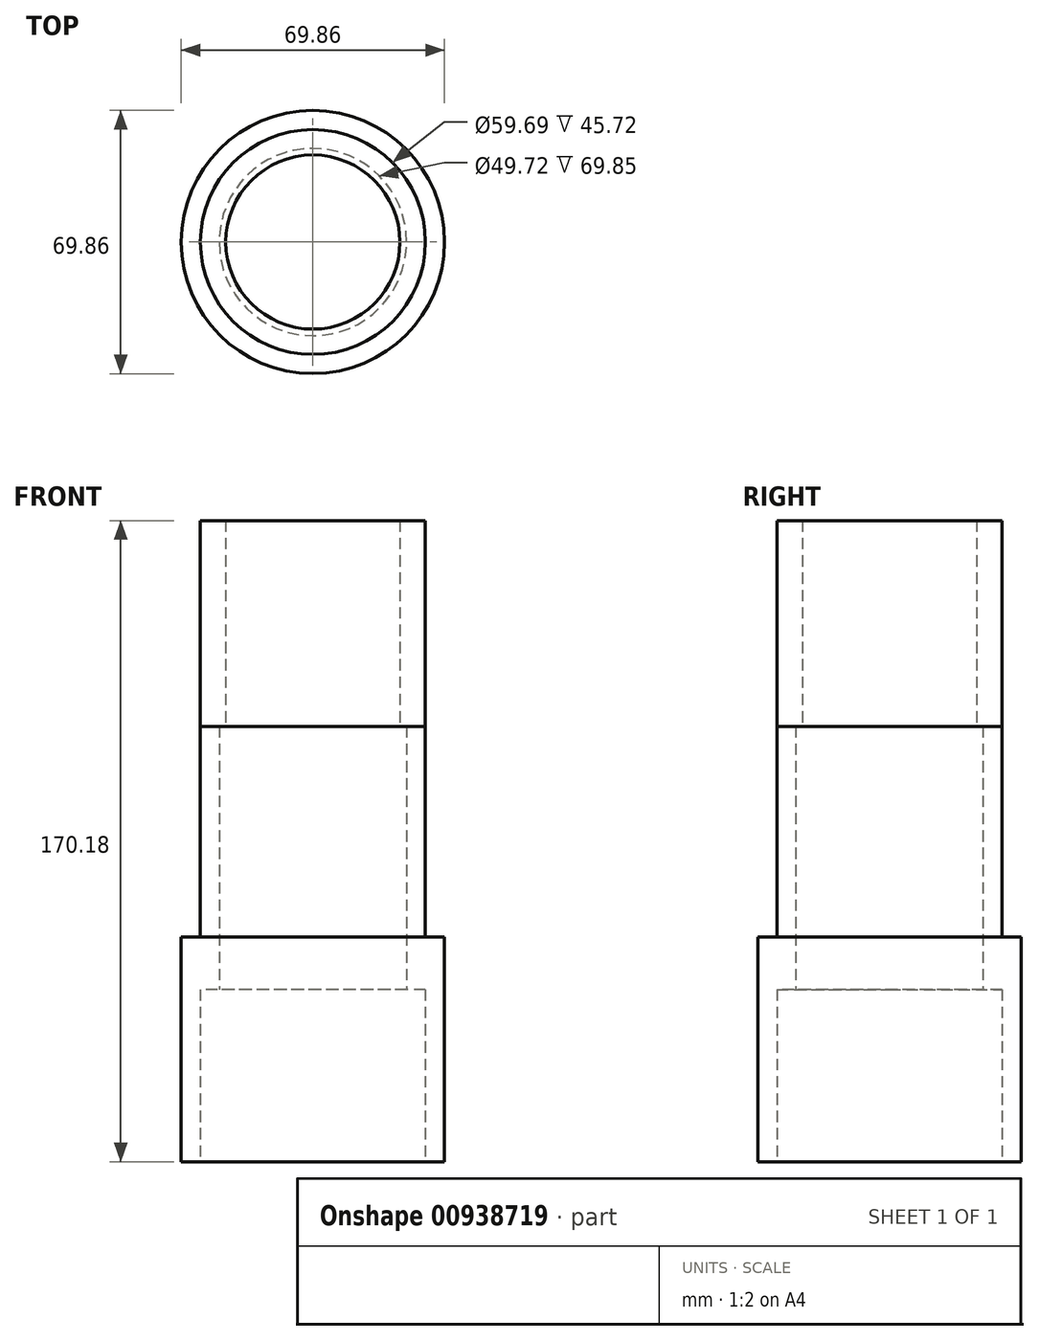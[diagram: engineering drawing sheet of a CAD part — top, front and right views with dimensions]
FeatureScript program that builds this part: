
annotation { "Feature Type Name" : "Feature", "Feature Type Description" : "" }
export const myFeature = defineFeature(function(context is Context, id is Id, definition is map)
    precondition{}
    {
        {
            var Q0;
            Q0=qCreatedBy(makeId("Top.planeOp"),FACE);
            var sketch = newSketch(context, id + "F0", { "sketchPlane" : qUnion([Q0])});
            skCircle(sketch, "E0", {"center": v(0, 0) * mm, "radius": 34.93 * mm});
            skCircle(sketch, "E1", {"center": v(0, 0) * mm, "radius": 29.85 * mm});
            skSolve(sketch);
        }
        {
            var Q0;
            Q0 = qSketchRegion(id + "F0", true);
            extrude(context, id + "F1", {"entities" : qUnion([Q0]), "depth" : 59.69 * mm, "offsetDistance" : 25.4 * mm});
        }
        {
            var Q0;
            Q0=qCreatedBy(makeId("Top.planeOp"),FACE);
            cPlane(context, id + "F2", {"entities" : qUnion([Q0]), "cplaneType" : CPlaneType.OFFSET, "offset" : 38.1 * mm, "width" : 152.4 * mm, "height" : 152.4 * mm});
        }
        {
            var Q0;
            Q0=qCreatedBy(makeId("Top.planeOp"),FACE);
            cPlane(context, id + "F3", {"entities" : qUnion([Q0]), "cplaneType" : CPlaneType.OFFSET, "offset" : 45.72 * mm, "width" : 152.4 * mm, "height" : 152.4 * mm});
        }
        {
            var Q0;
            Q0=qCreatedBy(id+"F2.planeOp",FACE);
            var sketch = newSketch(context, id + "F4", { "sketchPlane" : qUnion([Q0])});
            skCircle(sketch, "E2", {"center": v(0, 0) * mm, "radius": 29.84 * mm});
            skSolve(sketch);
        }
        {
            var Q0;
            Q0=qCreatedBy(id+"F3.planeOp",FACE);
            var sketch = newSketch(context, id + "F5", { "sketchPlane" : qUnion([Q0])});
            skCircle(sketch, "E3", {"center": v(0, 0) * mm, "radius": 24.77 * mm});
            skSolve(sketch);
        }
        {
            var Q0;
            Q0=sQuery(id+"F4.wireOp",EDGE,"E2");
            var Q1;
            Q1=sQuery(id+"F5.wireOp",EDGE,"E3");
            loft(context, id + "F6", {"bodyType" : ToolBodyType.SURFACE, "wireProfilesArray" : [{ "wireProfileEntities" : qUnion([Q0]) }, { "wireProfileEntities" : qUnion([Q1]) }]});
        }
        {
            var Q0;
            Q0=qCreatedBy(id+"F3.planeOp",FACE);
            var sketch = newSketch(context, id + "F7", { "sketchPlane" : qUnion([Q0])});
            skCircle(sketch, "E4", {"center": v(0, 0) * mm, "radius": 29.85 * mm});
            skCircle(sketch, "E5", {"center": v(0, 0) * mm, "radius": 24.86 * mm});
            skSolve(sketch);
        }
        {
            var Q0;
            Q0 = qSketchRegion(id + "F7", true);
            extrude(context, id + "F8", {"entities" : qUnion([Q0]), "operationType" : NewBodyOperationType.ADD, "depth" : 69.85 * mm, "offsetDistance" : 25.4 * mm});
        }
        {
            var Q0;
            Q0=qCreatedBy(makeId("Top.planeOp"),FACE);
            cPlane(context, id + "F9", {"entities" : qUnion([Q0]), "cplaneType" : CPlaneType.OFFSET, "offset" : 170.18 * mm, "width" : 152.4 * mm, "height" : 152.4 * mm});
        }
        {
            var Q0;
            Q0=qCreatedBy(id+"F9.planeOp",FACE);
            cPlane(context, id + "F10", {"entities" : qUnion([Q0]), "cplaneType" : CPlaneType.OFFSET, "offset" : 54.6 * mm, "oppositeDirection" : true, "width" : 152.4 * mm, "height" : 152.4 * mm});
        }
        {
            var Q0;
            Q0=qCreatedBy(id+"F10.planeOp",FACE);
            cPlane(context, id + "F11", {"entities" : qUnion([Q0]), "cplaneType" : CPlaneType.OFFSET, "offset" : 7.62 * mm, "oppositeDirection" : true, "width" : 152.4 * mm, "height" : 152.4 * mm});
        }
        {
            var Q0;
            Q0=qCreatedBy(id+"F11.planeOp",FACE);
            var sketch = newSketch(context, id + "F12", { "sketchPlane" : qUnion([Q0])});
            skCircle(sketch, "E6", {"center": v(0, 0) * mm, "radius": 24.77 * mm});
            skSolve(sketch);
        }
        {
            var Q0;
            Q0=qCreatedBy(id+"F10.planeOp",FACE);
            var sketch = newSketch(context, id + "F13", { "sketchPlane" : qUnion([Q0])});
            skCircle(sketch, "E7", {"center": v(0, 0) * mm, "radius": 23.11 * mm});
            skSolve(sketch);
        }
        {
            var Q0;
            Q0=sQuery(id+"F12.wireOp",EDGE,"E6");
            var Q1;
            Q1=sQuery(id+"F13.wireOp",EDGE,"E7");
            loft(context, id + "F14", {"bodyType" : ToolBodyType.SURFACE, "wireProfilesArray" : [{ "wireProfileEntities" : qUnion([Q0]) }, { "wireProfileEntities" : qUnion([Q1]) }]});
        }
        {
            var Q0;
            Q0=qCreatedBy(id+"F10.planeOp",FACE);
            var sketch = newSketch(context, id + "F15", { "sketchPlane" : qUnion([Q0])});
            skCircle(sketch, "E8", {"center": v(0, 0) * mm, "radius": 23.11 * mm});
            skCircle(sketch, "E9", {"center": v(0, 0) * mm, "radius": 29.85 * mm});
            skSolve(sketch);
        }
        {
            var Q0;
            Q0 = qSketchRegion(id + "F15", true);
            extrude(context, id + "F16", {"entities" : qUnion([Q0]), "depth" : 54.6 * mm, "offsetDistance" : 25.4 * mm});
        }
    });
